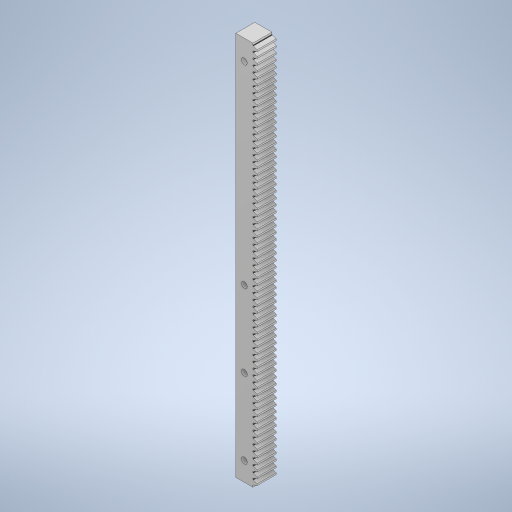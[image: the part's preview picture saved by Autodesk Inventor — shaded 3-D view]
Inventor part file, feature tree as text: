
AUTODESK INVENTOR PART (.ipt)
format: ipt  version: 2023 (Build 270158000, 158)  size: 3,068,928 bytes
history: native  units: mm
features: sketch x4, extrude x3, other x1, hole x1
ambient origin geometry x8: Origin, YZ Plane, XZ Plane, XY Plane, X Axis, Y Axis, Z Axis, Center Point
bodies: Body1 (feature_tree)
feature tree (9):
  other  "ソリッド1"
  extrude  "押し出し1"  Depth=10.0mm
  extrude  "押し出し12"  Depth=3.95363mm
  extrude  "押し出し13"  Depth=10.0mm
  hole  "穴3"  [1 undecoded]
  sketch  "スケッチ1"
  sketch  "スケッチ14"
  sketch  "スケッチ15"
  sketch  "スケッチ16"
note: 1 required parameter value undecoded (feature->parameter linkage not recoverable at this tier; creation-order binding heuristic only, values carry confidence <= 0.55)
